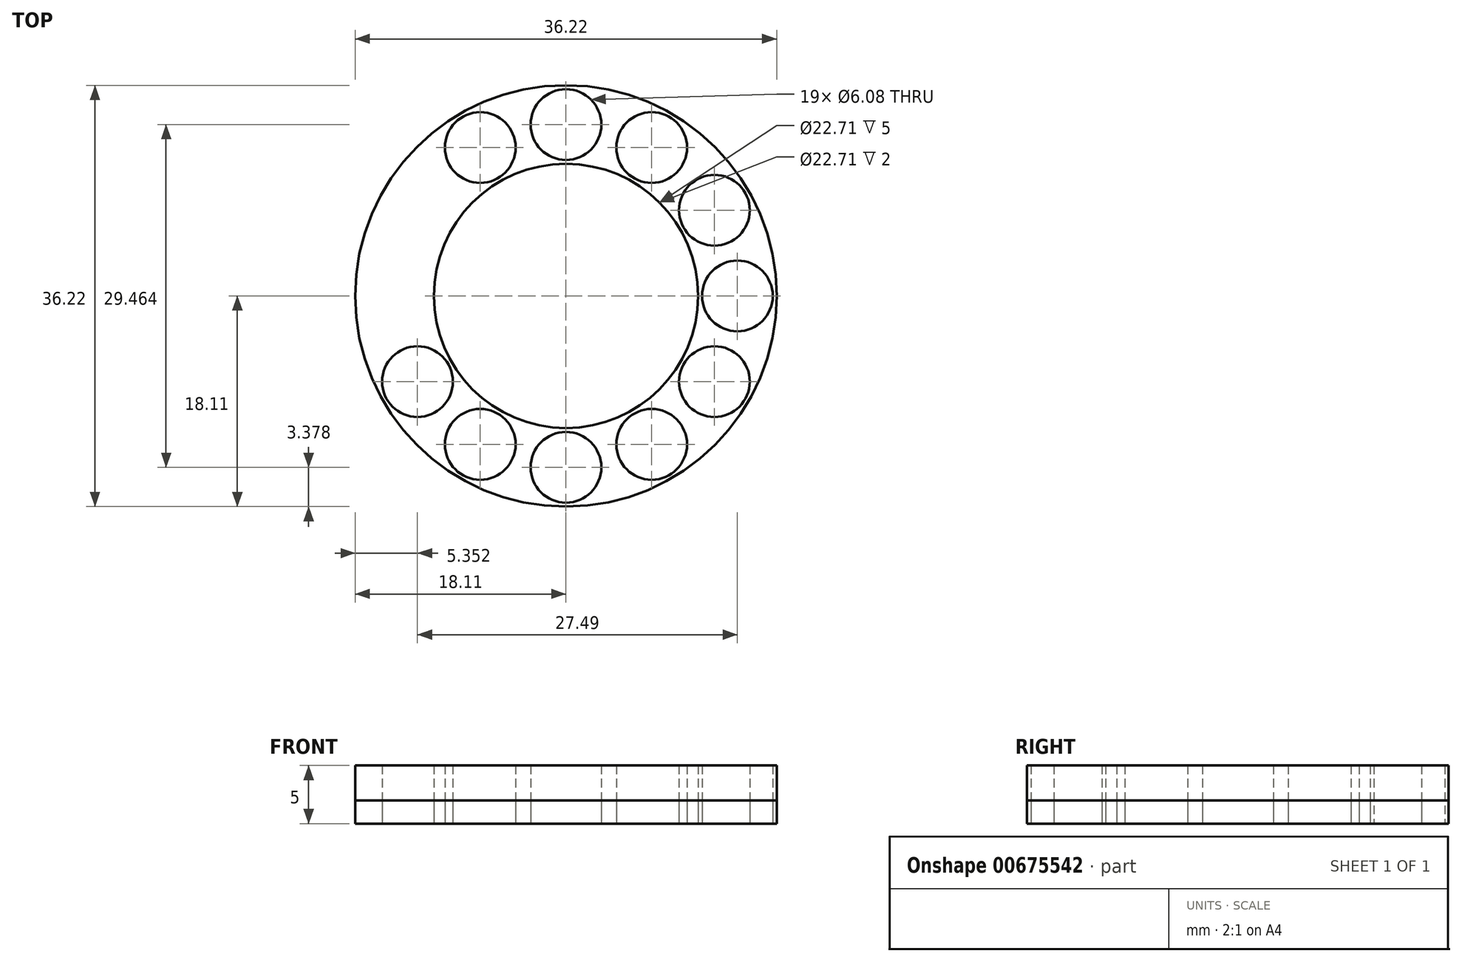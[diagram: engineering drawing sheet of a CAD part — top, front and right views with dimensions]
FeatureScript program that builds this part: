
annotation { "Feature Type Name" : "Feature", "Feature Type Description" : "" }
export const myFeature = defineFeature(function(context is Context, id is Id, definition is map)
    precondition{}
    {
        {
            var Q0;
            Q0=qCreatedBy(makeId("Top.planeOp"),FACE);
            var sketch = newSketch(context, id + "F0", { "sketchPlane" : qUnion([Q0])});
            skCircle(sketch, "E0", {"center": v(0, 14.73) * mm, "radius": 3.04 * mm});
            skCircle(sketch, "E1", {"center": v(7.37, 12.76) * mm, "radius": 3.04 * mm});
            skCircle(sketch, "E2", {"center": v(12.76, 7.37) * mm, "radius": 3.04 * mm});
            skCircle(sketch, "E3", {"center": v(14.73, 0) * mm, "radius": 3.04 * mm});
            skCircle(sketch, "E4", {"center": v(12.76, -7.37) * mm, "radius": 3.04 * mm});
            skCircle(sketch, "E5", {"center": v(7.37, -12.76) * mm, "radius": 3.04 * mm});
            skCircle(sketch, "E6", {"center": v(0, -14.73) * mm, "radius": 3.04 * mm});
            skCircle(sketch, "E7", {"center": v(-7.37, -12.76) * mm, "radius": 3.04 * mm});
            skCircle(sketch, "E8", {"center": v(-12.76, -7.37) * mm, "radius": 3.04 * mm});
            skCircle(sketch, "E9", {"center": v(-7.37, 12.76) * mm, "radius": 3.04 * mm});
            skCircle(sketch, "E10", {"center": v(-14.73, 0) * mm, "radius": 3.04 * mm});
            skCircle(sketch, "E11", {"center": v(0, 0) * mm, "radius": 11.36 * mm});
            skCircle(sketch, "E12", {"center": v(0, 0) * mm, "radius": 18.11 * mm});
            skCircle(sketch, "E13", {"center": v(-12.76, 7.3) * mm, "radius": 3.04 * mm});
            skSolve(sketch);
        }
        {
            var Q0;
            Q0=makeQuery(id+"F0.imprint","IMPRINT",FACE,{"disambiguationData":[TD([[makeQuery(id+"F0.imprint","IMPRINT",EDGE,{"derivedFrom":sQuery(id+"F0.wireOp",EDGE,"E13")}),1.0]])]});
            var Q1;
            Q1=makeQuery(id+"F0.imprint","IMPRINT",FACE,{"disambiguationData":[TD([[makeQuery(id+"F0.imprint","IMPRINT",EDGE,{"derivedFrom":sQuery(id+"F0.wireOp",EDGE,"E9")}),-1.0]])]});
            var Q2;
            Q2=makeQuery(id+"F0.imprint","IMPRINT",FACE,{"disambiguationData":[TD([[makeQuery(id+"F0.imprint","IMPRINT",EDGE,{"derivedFrom":sQuery(id+"F0.wireOp",EDGE,"E0")}),-1.0]])]});
            var Q3;
            Q3=makeQuery(id+"F0.imprint","IMPRINT",FACE,{"disambiguationData":[TD([[makeQuery(id+"F0.imprint","IMPRINT",EDGE,{"derivedFrom":sQuery(id+"F0.wireOp",EDGE,"E1")}),-1.0]])]});
            var Q4;
            Q4=makeQuery(id+"F0.imprint","IMPRINT",FACE,{"disambiguationData":[TD([[makeQuery(id+"F0.imprint","IMPRINT",EDGE,{"derivedFrom":sQuery(id+"F0.wireOp",EDGE,"E2")}),-1.0]])]});
            var Q5;
            Q5=makeQuery(id+"F0.imprint","IMPRINT",FACE,{"disambiguationData":[TD([[makeQuery(id+"F0.imprint","IMPRINT",EDGE,{"derivedFrom":sQuery(id+"F0.wireOp",EDGE,"E3")}),-1.0]])]});
            var Q6;
            Q6=makeQuery(id+"F0.imprint","IMPRINT",FACE,{"disambiguationData":[TD([[makeQuery(id+"F0.imprint","IMPRINT",EDGE,{"derivedFrom":sQuery(id+"F0.wireOp",EDGE,"E4")}),-1.0]])]});
            var Q7;
            Q7=makeQuery(id+"F0.imprint","IMPRINT",FACE,{"disambiguationData":[TD([[makeQuery(id+"F0.imprint","IMPRINT",EDGE,{"derivedFrom":sQuery(id+"F0.wireOp",EDGE,"E5")}),-1.0]])]});
            var Q8;
            Q8=makeQuery(id+"F0.imprint","IMPRINT",FACE,{"disambiguationData":[TD([[makeQuery(id+"F0.imprint","IMPRINT",EDGE,{"derivedFrom":sQuery(id+"F0.wireOp",EDGE,"E6")}),-1.0]])]});
            var Q9;
            Q9=makeQuery(id+"F0.imprint","IMPRINT",FACE,{"disambiguationData":[TD([[makeQuery(id+"F0.imprint","IMPRINT",EDGE,{"derivedFrom":sQuery(id+"F0.wireOp",EDGE,"E7")}),-1.0]])]});
            var Q10;
            Q10=makeQuery(id+"F0.imprint","IMPRINT",FACE,{"disambiguationData":[TD([[makeQuery(id+"F0.imprint","IMPRINT",EDGE,{"derivedFrom":sQuery(id+"F0.wireOp",EDGE,"E8")}),-1.0]])]});
            var Q11;
            Q11=makeQuery(id+"F0.imprint","IMPRINT",FACE,{"disambiguationData":[TD([[makeQuery(id+"F0.imprint","IMPRINT",EDGE,{"derivedFrom":sQuery(id+"F0.wireOp",EDGE,"E10")}),1.0]])]});
            var Q12;
            Q12=makeQuery(id+"F0.imprint","IMPRINT",FACE,{"disambiguationData":[TD([[makeQuery(id+"F0.imprint","IMPRINT",EDGE,{"derivedFrom":sQuery(id+"F0.wireOp",EDGE,"E0")}),1.0]])]});
            extrude(context, id + "F1", {"entities" : qUnion([Q0, Q1, Q2, Q3, Q4, Q5, Q6, Q7, Q8, Q9, Q10, Q11, Q12]), "depth" : 2 * mm, "offsetDistance" : 25 * mm});
        }
        {
            var Q0;
            Q0=makeQuery(id+"F0.imprint","IMPRINT",FACE,{"disambiguationData":[TD([[makeQuery(id+"F0.imprint","IMPRINT",EDGE,{"derivedFrom":sQuery(id+"F0.wireOp",EDGE,"E9")}),-1.0]])]});
            var Q1;
            Q1=makeQuery(id+"F0.imprint","IMPRINT",FACE,{"disambiguationData":[TD([[makeQuery(id+"F0.imprint","IMPRINT",EDGE,{"derivedFrom":sQuery(id+"F0.wireOp",EDGE,"E0")}),-1.0]])]});
            var Q2;
            Q2=makeQuery(id+"F0.imprint","IMPRINT",FACE,{"disambiguationData":[TD([[makeQuery(id+"F0.imprint","IMPRINT",EDGE,{"derivedFrom":sQuery(id+"F0.wireOp",EDGE,"E1")}),-1.0]])]});
            var Q3;
            Q3=makeQuery(id+"F0.imprint","IMPRINT",FACE,{"disambiguationData":[TD([[makeQuery(id+"F0.imprint","IMPRINT",EDGE,{"derivedFrom":sQuery(id+"F0.wireOp",EDGE,"E2")}),-1.0]])]});
            var Q4;
            Q4=makeQuery(id+"F0.imprint","IMPRINT",FACE,{"disambiguationData":[TD([[makeQuery(id+"F0.imprint","IMPRINT",EDGE,{"derivedFrom":sQuery(id+"F0.wireOp",EDGE,"E3")}),-1.0]])]});
            var Q5;
            Q5=makeQuery(id+"F0.imprint","IMPRINT",FACE,{"disambiguationData":[TD([[makeQuery(id+"F0.imprint","IMPRINT",EDGE,{"derivedFrom":sQuery(id+"F0.wireOp",EDGE,"E4")}),-1.0]])]});
            var Q6;
            Q6=makeQuery(id+"F0.imprint","IMPRINT",FACE,{"disambiguationData":[TD([[makeQuery(id+"F0.imprint","IMPRINT",EDGE,{"derivedFrom":sQuery(id+"F0.wireOp",EDGE,"E5")}),-1.0]])]});
            var Q7;
            Q7=makeQuery(id+"F0.imprint","IMPRINT",FACE,{"disambiguationData":[TD([[makeQuery(id+"F0.imprint","IMPRINT",EDGE,{"derivedFrom":sQuery(id+"F0.wireOp",EDGE,"E6")}),-1.0]])]});
            var Q8;
            Q8=makeQuery(id+"F0.imprint","IMPRINT",FACE,{"disambiguationData":[TD([[makeQuery(id+"F0.imprint","IMPRINT",EDGE,{"derivedFrom":sQuery(id+"F0.wireOp",EDGE,"E7")}),-1.0]])]});
            var Q9;
            Q9=makeQuery(id+"F0.imprint","IMPRINT",FACE,{"disambiguationData":[TD([[makeQuery(id+"F0.imprint","IMPRINT",EDGE,{"derivedFrom":sQuery(id+"F0.wireOp",EDGE,"E8")}),-1.0]])]});
            var Q10;
            Q10=makeQuery(id+"F0.imprint","IMPRINT",FACE,{"disambiguationData":[TD([[makeQuery(id+"F0.imprint","IMPRINT",EDGE,{"derivedFrom":sQuery(id+"F0.wireOp",EDGE,"E10")}),1.0]])]});
            var Q11;
            Q11=makeQuery(id+"F0.imprint","IMPRINT",FACE,{"disambiguationData":[TD([[makeQuery(id+"F0.imprint","IMPRINT",EDGE,{"derivedFrom":sQuery(id+"F0.wireOp",EDGE,"E13")}),1.0]])]});
            extrude(context, id + "F2", {"entities" : qUnion([Q0, Q1, Q2, Q3, Q4, Q5, Q6, Q7, Q8, Q9, Q10, Q11]), "depth" : 5 * mm, "offsetDistance" : 25 * mm});
        }
    });
